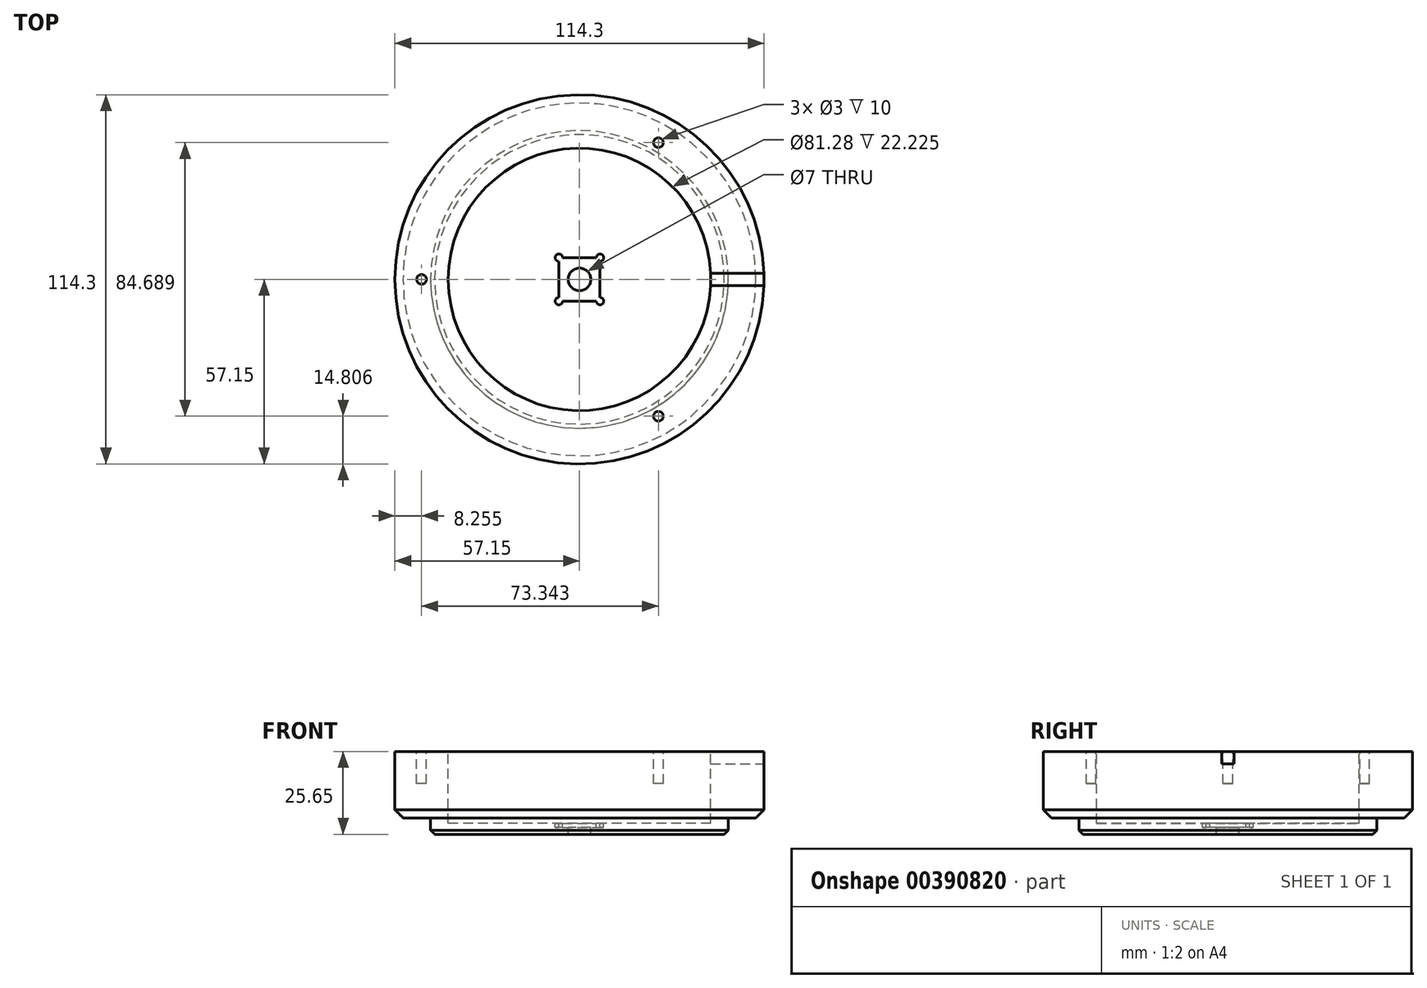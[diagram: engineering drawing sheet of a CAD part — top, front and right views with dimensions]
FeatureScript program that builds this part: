
annotation { "Feature Type Name" : "Feature", "Feature Type Description" : "" }
export const myFeature = defineFeature(function(context is Context, id is Id, definition is map)
    precondition{}
    {
        {
            var Q0;
            Q0=qCreatedBy(makeId("Front.planeOp"),FACE);
            var sketch = newSketch(context, id + "F0", { "sketchPlane" : qUnion([Q0])});
            skLineSegment(sketch, "E0", {"start": v(-57.15, 0) * mm, "end": v(-57.15, -20.57) * mm});
            skLineSegment(sketch, "E1", {"start": v(-46.1, -25.65) * mm, "end": v(-3.5, -25.65) * mm});
            skLineSegment(sketch, "E2", {"start": v(-57.15, 0) * mm, "end": v(-40.64, 0) * mm});
            skLineSegment(sketch, "E3", {"start": v(-40.64, 0) * mm, "end": v(-40.64, -22.23) * mm});
            skLineSegment(sketch, "E4", {"start": v(-40.64, -22.23) * mm, "end": v(-3.5, -22.22) * mm});
            skLineSegment(sketch, "E5", {"start": v(0, 61.82) * mm, "end": v(0, -22.22) * mm, "construction": true});
            skLineSegment(sketch, "E6", {"start": v(-3.5, -25.65) * mm, "end": v(-3.5, -22.22) * mm});
            skLineSegment(sketch, "E7.trimOffspring", {"start": v(0, -25.65) * mm, "end": v(0, -64.13) * mm, "construction": true});
            skLineSegment(sketch, "E8", {"start": v(-57.15, -20.57) * mm, "end": v(-46.1, -20.57) * mm});
            skLineSegment(sketch, "E9", {"start": v(-46.1, -20.57) * mm, "end": v(-46.1, -25.65) * mm});
            skSolve(sketch);
        }
        {
            var Q0;
            Q0 = qSketchRegion(id + "F0", true);
            var Q1;
            Q1=sQuery(id+"F0.wireOp",EDGE,"E5");
            revolve(context, id + "F1", {"entities" : qUnion([Q0]), "axis" : qUnion([Q1]), "revolveType" : RevolveType.FULL});
        }
        {
            var Q0;
            Q0=makeQuery(id+"F1.opRevolve","SWEPT_EDGE",EDGE,{"disambiguationData":[OSD([sQuery(id+"F0.wireOp",EDGE,"E0"),sQuery(id+"F0.wireOp",EDGE,"E8")])]});
            chamfer(context, id + "F2", {"entities" : qUnion([Q0]), "width" : 2.54 * mm, "tangentPropagation" : true});
        }
        {
            var Q0;
            Q0=makeQuery(id+"F1.opRevolve","SWEPT_EDGE",EDGE,{"disambiguationData":[OSD([sQuery(id+"F0.wireOp",EDGE,"E1"),sQuery(id+"F0.wireOp",EDGE,"E9")])]});
            chamfer(context, id + "F3", {"entities" : qUnion([Q0]), "width" : 1.27 * mm, "tangentPropagation" : true});
        }
        {
            var Q0;
            Q0=makeQuery(id+"F1.opRevolve","SWEPT_FACE",FACE,{"disambiguationData":[OSD([sQuery(id+"F0.wireOp",EDGE,"E4")])]});
            var sketch = newSketch(context, id + "F4", { "sketchPlane" : qUnion([Q0])});
            skLineSegment(sketch, "E10.bottom", {"start": v(-5.23, 6.73) * mm, "end": v(5.23, 6.73) * mm});
            skLineSegment(sketch, "E10.top", {"start": v(-5.23, -6.73) * mm, "end": v(5.23, -6.73) * mm});
            skLineSegment(sketch, "E10.left", {"start": v(-6.38, 5.59) * mm, "end": v(-6.38, -5.59) * mm});
            skLineSegment(sketch, "E10.right", {"start": v(6.38, 5.59) * mm, "end": v(6.38, -5.59) * mm});
            skPoint(sketch, "E10.middle", {"position": v(0, 0) * mm});
            skArc(sketch, "E11", {"start": v(-5.23, 6.73) * mm, "mid": v(-7.18, 7.54) * mm, "end": v(-6.38, 5.59) * mm});
            skArc(sketch, "E12.1.0.0", {"start": v(6.38, 5.59) * mm, "mid": v(7.18, 7.54) * mm, "end": v(5.23, 6.73) * mm});
            skLineSegment(sketch, "E12.direction1", {"start": v(-5.23, 6.73) * mm, "end": v(5.23, 6.73) * mm, "construction": true});
            skArc(sketch, "E13.1.0.0", {"start": v(-6.38, -5.59) * mm, "mid": v(-7.18, -7.54) * mm, "end": v(-5.23, -6.73) * mm});
            skArc(sketch, "E13.1.0.1", {"start": v(5.23, -6.73) * mm, "mid": v(7.18, -7.54) * mm, "end": v(6.38, -5.59) * mm});
            skLineSegment(sketch, "E13.direction1", {"start": v(-6.38, 5.59) * mm, "end": v(-6.38, -5.59) * mm, "construction": true});
            skLineSegment(sketch, "E14.trimOffspring", {"start": v(-6.38, -6.73) * mm, "end": v(-6.38, -6.73) * mm});
            skSolve(sketch);
        }
        {
            var Q0;
            Q0 = qSketchRegion(id + "F4", true);
            extrude(context, id + "F5", {"entities" : qUnion([Q0]), "operationType" : NewBodyOperationType.REMOVE, "oppositeDirection" : true, "depth" : 1.27 * mm});
        }
        {
            var Q0;
            Q0=makeQuery(id+"F1.opRevolve","SWEPT_FACE",FACE,{"disambiguationData":[OSD([sQuery(id+"F0.wireOp",EDGE,"E2")])]});
            var sketch = newSketch(context, id + "F6", { "sketchPlane" : qUnion([Q0])});
            skCircle(sketch, "E15", {"center": v(-48.9, 0) * mm, "radius": 1.5 * mm});
            skLineSegment(sketch, "E16", {"start": v(-40.64, 0) * mm, "end": v(-57.15, 0) * mm, "construction": true});
            skCircle(sketch, "E17.1.0", {"center": v(24.45, -42.34) * mm, "radius": 1.5 * mm});
            skCircle(sketch, "E17.2.0", {"center": v(24.45, 42.34) * mm, "radius": 1.5 * mm});
            skPoint(sketch, "E17.center", {"position": v(0, 0) * mm});
            skCircle(sketch, "E18", {"center": v(0, 0) * mm, "radius": 48.9 * mm, "construction": true});
            skSolve(sketch);
        }
        {
            var Q0;
            Q0 = qSketchRegion(id + "F6", true);
            extrude(context, id + "F7", {"entities" : qUnion([Q0]), "operationType" : NewBodyOperationType.REMOVE, "oppositeDirection" : true, "depth" : 10 * mm});
        }
        {
            var Q0;
            Q0=makeQuery(id+"F1.opRevolve","SWEPT_FACE",FACE,{"disambiguationData":[OSD([sQuery(id+"F0.wireOp",EDGE,"E2")])]});
            var sketch = newSketch(context, id + "F8", { "sketchPlane" : qUnion([Q0])});
            skLineSegment(sketch, "E19.bottom", {"start": v(32.86, 1.9) * mm, "end": v(65.28, 1.9) * mm});
            skLineSegment(sketch, "E19.top", {"start": v(32.86, -1.9) * mm, "end": v(65.28, -1.9) * mm});
            skLineSegment(sketch, "E19.left", {"start": v(32.86, 1.9) * mm, "end": v(32.86, -1.9) * mm});
            skLineSegment(sketch, "E19.right", {"start": v(65.28, 1.9) * mm, "end": v(65.28, -1.9) * mm});
            skLineSegment(sketch, "E20", {"start": v(-17.28, 0) * mm, "end": v(87.81, 0) * mm, "construction": true});
            skSolve(sketch);
        }
        {
            var Q0;
            Q0 = qSketchRegion(id + "F8", true);
            extrude(context, id + "F9", {"entities" : qUnion([Q0]), "operationType" : NewBodyOperationType.REMOVE, "oppositeDirection" : true, "depth" : 3.8 * mm});
        }
    });
